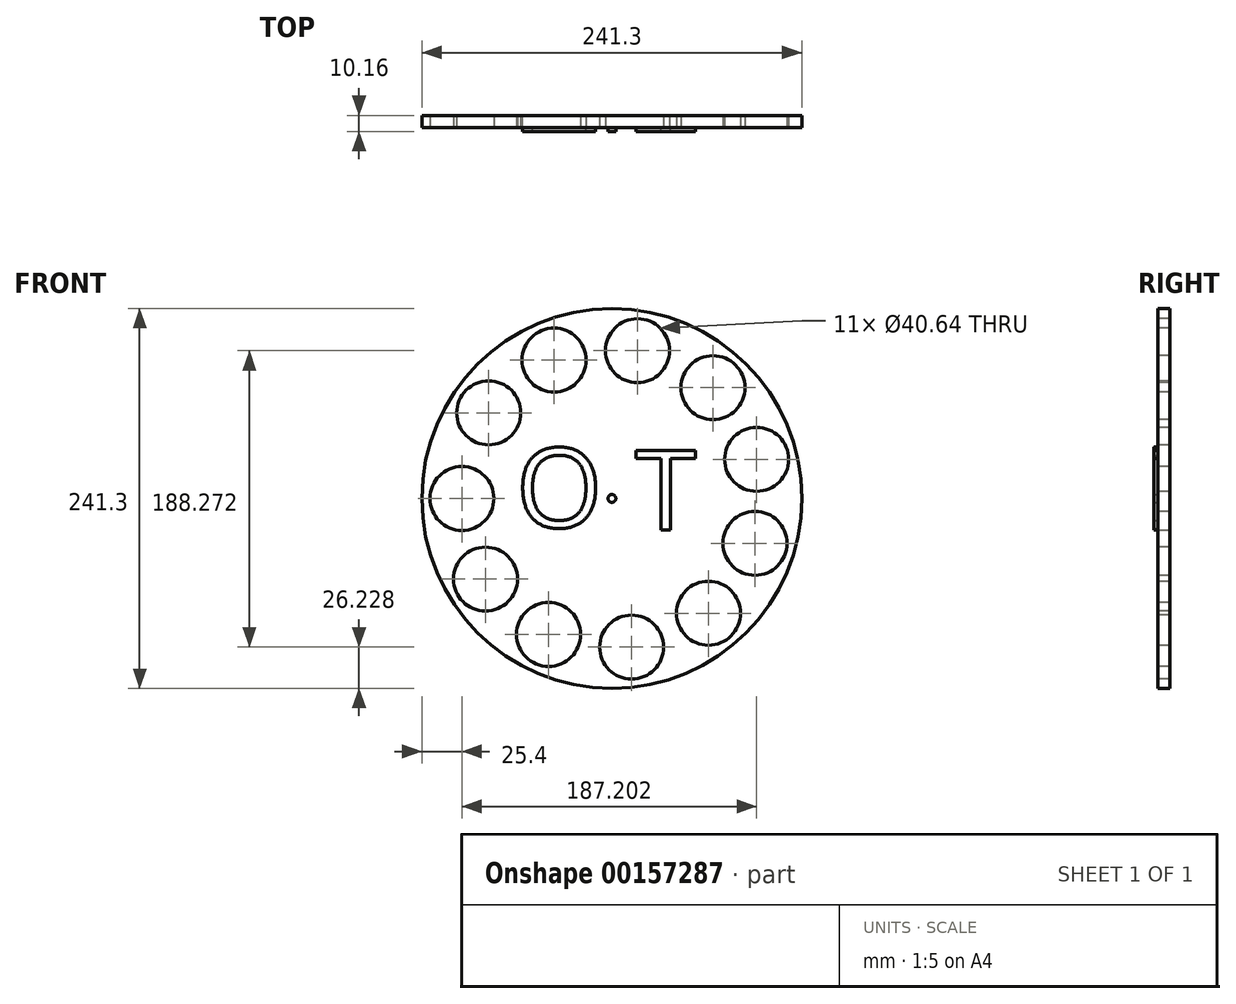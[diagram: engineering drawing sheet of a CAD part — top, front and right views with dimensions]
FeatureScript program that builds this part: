
annotation { "Feature Type Name" : "Feature", "Feature Type Description" : "" }
export const myFeature = defineFeature(function(context is Context, id is Id, definition is map)
    precondition{}
    {
        {
            var Q0;
            Q0=qCreatedBy(makeId("Front.planeOp"),FACE);
            var sketch = newSketch(context, id + "F0", { "sketchPlane" : qUnion([Q0])});
            skCircle(sketch, "E0", {"center": v(0, 0) * mm, "radius": 120.65 * mm});
            skSolve(sketch);
        }
        {
            var Q0;
            Q0 = qSketchRegion(id + "F0", true);
            extrude(context, id + "F1", {"entities" : qUnion([Q0]), "depth" : 7.62 * mm});
        }
        {
            var Q0;
            Q0=makeQuery(id+"F1.opExtrude","CAP_FACE",FACE,{"disambiguationData":[OSD([sQuery(id+"F0.wireOp",EDGE,"E0")])],"isStart":false});
            var sketch = newSketch(context, id + "F2", { "sketchPlane" : qUnion([Q0])});
            skCircle(sketch, "E1", {"center": v(16.27, 93.85) * mm, "radius": 20.32 * mm});
            skCircle(sketch, "E2", {"center": v(64.17, 70.39) * mm, "radius": 20.32 * mm});
            skCircle(sketch, "E3", {"center": v(91.95, 24.85) * mm, "radius": 20.32 * mm});
            skCircle(sketch, "E4", {"center": v(90.9, -28.48) * mm, "radius": 20.32 * mm});
            skCircle(sketch, "E5", {"center": v(-36.73, 87.88) * mm, "radius": 20.32 * mm});
            skCircle(sketch, "E6", {"center": v(-80.31, -51.2) * mm, "radius": 20.32 * mm});
            skCircle(sketch, "E7", {"center": v(-40.2, -86.35) * mm, "radius": 20.32 * mm});
            skCircle(sketch, "E8", {"center": v(12.53, -94.42) * mm, "radius": 20.32 * mm});
            skCircle(sketch, "E9", {"center": v(61.33, -72.88) * mm, "radius": 20.32 * mm});
            skCircle(sketch, "E10", {"center": v(-95.25, 0) * mm, "radius": 20.32 * mm});
            skCircle(sketch, "E11", {"center": v(-78.22, 54.35) * mm, "radius": 20.32 * mm});
            skSolve(sketch);
        }
        {
            var Q0;
            Q0 = qSketchRegion(id + "F2", true);
            extrude(context, id + "F3", {"entities" : qUnion([Q0]), "operationType" : NewBodyOperationType.REMOVE, "oppositeDirection" : true, "depth" : 25.4 * mm});
        }
        {
            var Q0;
            Q0=makeQuery(id+"F1.opExtrude","CAP_FACE",FACE,{"disambiguationData":[OSD([sQuery(id+"F0.wireOp",EDGE,"E0")])],"isStart":false});
            var sketch = newSketch(context, id + "F4", { "sketchPlane" : qUnion([Q0])});
            skPoint(sketch, "E12", {"position": v(0, 0) * mm});
            skText(sketch, "E13", { "text": "O", "fontName": "OpenSans-Regular.ttf"});
            skText(sketch, "E14", { "text": "T", "fontName": "OpenSans-Regular.ttf"});
            const initialGuessF4  = {"E13": [-0.06096, -0.0185, 1, 0, 0.0508], "E14": [0.01471, -0.01988, 1, 0, 0.0508]};
            skSetInitialGuess(sketch, initialGuessF4);
            skSolve(sketch);
        }
        {
            var Q0;
            Q0 = qSketchRegion(id + "F4", true);
            extrude(context, id + "F5", {"entities" : qUnion([Q0]), "operationType" : NewBodyOperationType.ADD, "depth" : 2.54 * mm});
        }
        {
            var Q0;
            {var subQ0=sQuery(id+"F0.wireOp",EDGE,"E0");Q0=makeQuery(id+"F5.boolean.opBoolean","SPLIT",FACE,{"disambiguationData":[TD([makeQuery(id+"F1.opExtrude","SWEPT_FACE",FACE,{"disambiguationData":[OSD([subQ0])]})])],"derivedFrom":makeQuery(id+"F1.opExtrude","CAP_FACE",FACE,{"disambiguationData":[OSD([subQ0])],"isStart":false})});}
            var sketch = newSketch(context, id + "F6", { "sketchPlane" : qUnion([Q0])});
            skCircle(sketch, "E15", {"center": v(0, 0) * mm, "radius": 2.48 * mm});
            skSolve(sketch);
        }
        {
            var Q0;
            Q0 = qSketchRegion(id + "F6", true);
            extrude(context, id + "F7", {"entities" : qUnion([Q0]), "operationType" : NewBodyOperationType.ADD, "depth" : 2.54 * mm});
        }
    });
